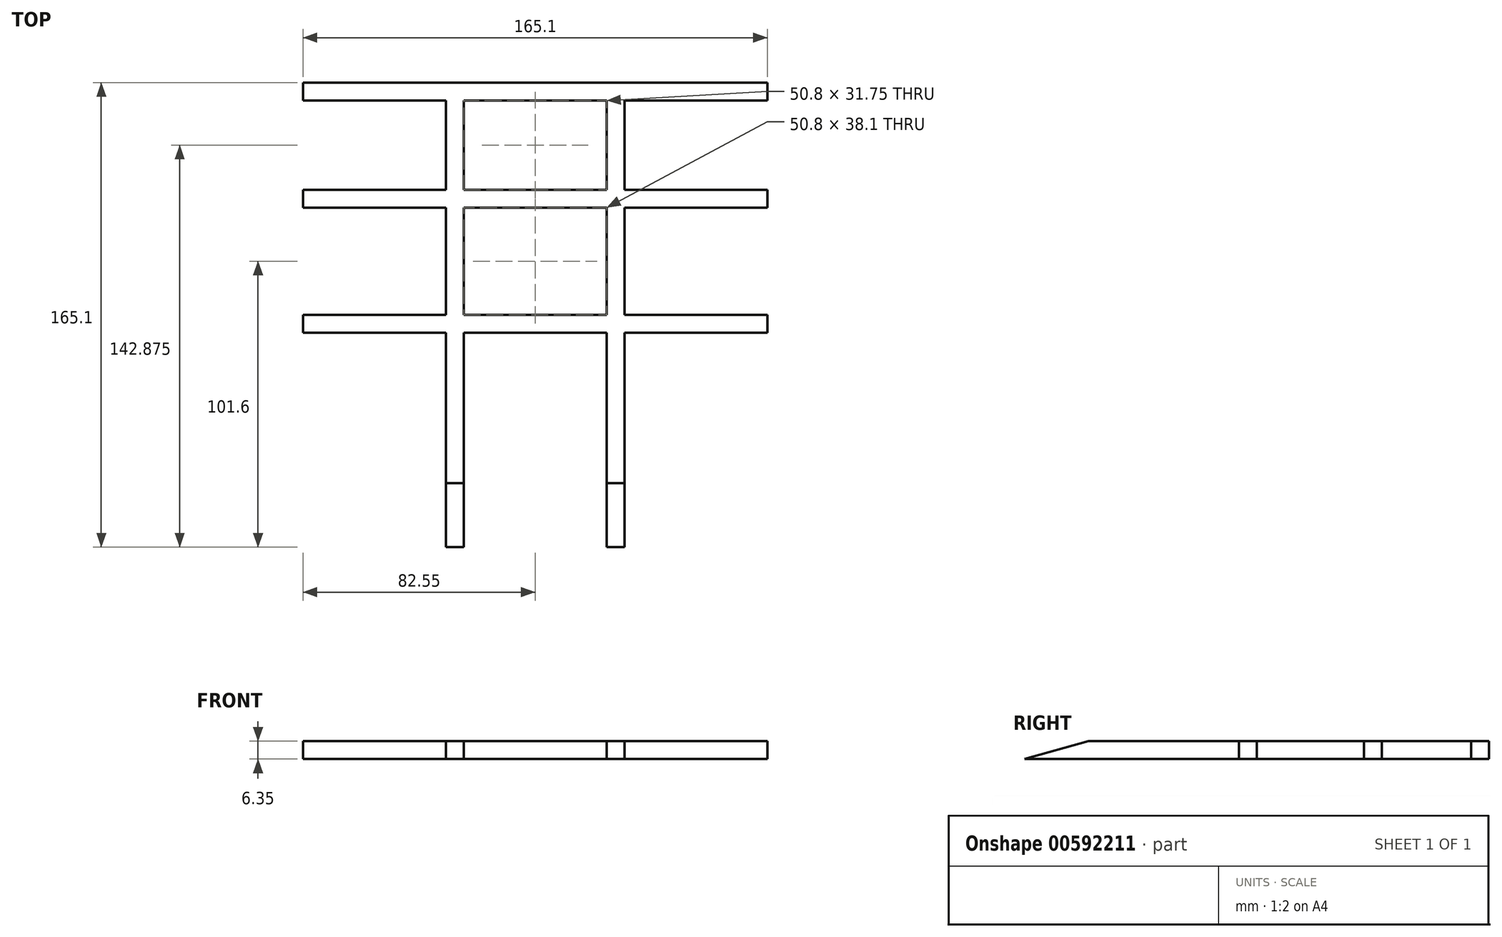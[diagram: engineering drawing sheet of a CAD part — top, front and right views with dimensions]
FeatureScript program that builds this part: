
annotation { "Feature Type Name" : "Feature", "Feature Type Description" : "" }
export const myFeature = defineFeature(function(context is Context, id is Id, definition is map)
    precondition{}
    {
        {
            var Q0;
            Q0=qCreatedBy(makeId("Top.planeOp"),FACE);
            var sketch = newSketch(context, id + "F0", { "sketchPlane" : qUnion([Q0])});
            skLineSegment(sketch, "E0.bottom", {"start": v(0, 0) * mm, "end": v(6.35, 0) * mm});
            skLineSegment(sketch, "E0.top", {"start": v(0, -76.2) * mm, "end": v(6.35, -76.2) * mm});
            skLineSegment(sketch, "E0.left", {"start": v(0, 0) * mm, "end": v(0, -76.2) * mm});
            skLineSegment(sketch, "E0.right", {"start": v(6.35, 0) * mm, "end": v(6.35, -76.2) * mm});
            skLineSegment(sketch, "E1.bottom", {"start": v(0, 0) * mm, "end": v(-50.8, 0) * mm});
            skLineSegment(sketch, "E1.top", {"start": v(0, 6.35) * mm, "end": v(-50.8, 6.35) * mm});
            skLineSegment(sketch, "E1.left", {"start": v(0, 0) * mm, "end": v(0, 6.35) * mm});
            skLineSegment(sketch, "E1.right", {"start": v(-50.8, 0) * mm, "end": v(-50.8, 6.35) * mm});
            skPoint(sketch, "E2.oppositeSnap0", {"position": v(3.18, -76.2) * mm});
            skLineSegment(sketch, "E2.bottom", {"start": v(-50.8, 0) * mm, "end": v(-57.15, 0) * mm});
            skLineSegment(sketch, "E2.top", {"start": v(-50.8, -76.2) * mm, "end": v(-57.15, -76.2) * mm});
            skLineSegment(sketch, "E2.left", {"start": v(-50.8, 0) * mm, "end": v(-50.8, -76.2) * mm});
            skLineSegment(sketch, "E2.right", {"start": v(-57.15, 0) * mm, "end": v(-57.15, -76.2) * mm});
            skLineSegment(sketch, "E3.bottom", {"start": v(-57.15, 0) * mm, "end": v(-107.95, 0) * mm});
            skLineSegment(sketch, "E3.top", {"start": v(-57.15, 6.35) * mm, "end": v(-107.95, 6.35) * mm});
            skLineSegment(sketch, "E3.left", {"start": v(-57.15, 0) * mm, "end": v(-57.15, 6.35) * mm});
            skLineSegment(sketch, "E3.right", {"start": v(-107.95, 0) * mm, "end": v(-107.95, 6.35) * mm});
            skLineSegment(sketch, "E4.bottom", {"start": v(6.35, 0) * mm, "end": v(57.15, 0) * mm});
            skLineSegment(sketch, "E4.top", {"start": v(6.35, 6.35) * mm, "end": v(57.15, 6.35) * mm});
            skLineSegment(sketch, "E4.left", {"start": v(6.35, 0) * mm, "end": v(6.35, 6.35) * mm});
            skLineSegment(sketch, "E4.right", {"start": v(57.15, 0) * mm, "end": v(57.15, 6.35) * mm});
            skLineSegment(sketch, "E5.bottom", {"start": v(-57.15, 6.35) * mm, "end": v(-50.8, 6.35) * mm});
            skLineSegment(sketch, "E5.top", {"start": v(-57.15, 44.45) * mm, "end": v(-50.8, 44.45) * mm});
            skLineSegment(sketch, "E5.left", {"start": v(-57.15, 6.35) * mm, "end": v(-57.15, 44.45) * mm});
            skLineSegment(sketch, "E5.right", {"start": v(-50.8, 6.35) * mm, "end": v(-50.8, 44.45) * mm});
            skLineSegment(sketch, "E6.bottom", {"start": v(0, 6.35) * mm, "end": v(6.35, 6.35) * mm});
            skLineSegment(sketch, "E6.top", {"start": v(0, 44.45) * mm, "end": v(6.35, 44.45) * mm});
            skLineSegment(sketch, "E6.left", {"start": v(0, 6.35) * mm, "end": v(0, 44.45) * mm});
            skLineSegment(sketch, "E6.right", {"start": v(6.35, 6.35) * mm, "end": v(6.35, 44.45) * mm});
            skLineSegment(sketch, "E7.bottom", {"start": v(-107.95, 44.45) * mm, "end": v(57.15, 44.45) * mm});
            skLineSegment(sketch, "E7.top", {"start": v(-107.95, 50.8) * mm, "end": v(57.15, 50.8) * mm});
            skLineSegment(sketch, "E7.left", {"start": v(-107.95, 44.45) * mm, "end": v(-107.95, 50.8) * mm});
            skLineSegment(sketch, "E7.right", {"start": v(57.15, 44.45) * mm, "end": v(57.15, 50.8) * mm});
            skLineSegment(sketch, "E8.MirrorCS", {"start": v(-57.15, 82.55) * mm, "end": v(-57.15, 44.45) * mm});
            skLineSegment(sketch, "E9.MirrorCS", {"start": v(-50.8, 82.55) * mm, "end": v(-50.8, 44.45) * mm});
            skLineSegment(sketch, "E10.MirrorCS", {"start": v(0, 82.55) * mm, "end": v(0, 44.45) * mm});
            skLineSegment(sketch, "E11.MirrorCS", {"start": v(6.35, 82.55) * mm, "end": v(6.35, 44.45) * mm});
            skLineSegment(sketch, "E12.MirrorCS", {"start": v(-57.15, 82.55) * mm, "end": v(-50.8, 82.55) * mm});
            skLineSegment(sketch, "E13.MirrorCS", {"start": v(0, 82.55) * mm, "end": v(6.35, 82.55) * mm});
            skLineSegment(sketch, "E14.bottom", {"start": v(-107.95, 82.55) * mm, "end": v(57.15, 82.55) * mm});
            skLineSegment(sketch, "E14.top", {"start": v(-107.95, 88.9) * mm, "end": v(57.15, 88.9) * mm});
            skLineSegment(sketch, "E14.left", {"start": v(-107.95, 82.55) * mm, "end": v(-107.95, 88.9) * mm});
            skLineSegment(sketch, "E14.right", {"start": v(57.15, 82.55) * mm, "end": v(57.15, 88.9) * mm});
            skSolve(sketch);
        }
        {
            var Q0;
            Q0=makeQuery(id+"F0.imprint","IMPRINT",FACE,{"disambiguationData":[TD([[makeQuery(id+"F0.imprint","IMPRINT",EDGE,{"derivedFrom":sQuery(id+"F0.wireOp",EDGE,"E14.top")}),-1.0]])]});
            var Q1;
            {var subQ0=sQuery(id+"F0.wireOp",EDGE,"E8.MirrorCS");var subQ1=sQuery(id+"F0.wireOp",EDGE,"E7.top");var subQ2=makeQuery(id+"F0.imprint","INTERSECT",VERTEX,{"derivedFrom":[subQ1,subQ0]});Q1=makeQuery(id+"F0.imprint","IMPRINT",FACE,{"disambiguationData":[TD([[makeQuery(id+"F0.imprint","IMPRINT",EDGE,{"disambiguationData":[TD([[subQ2,-1.0]])],"derivedFrom":subQ1}),1.0]])]});}
            var Q2;
            {var subQ0=sQuery(id+"F0.wireOp",EDGE,"E11.MirrorCS");var subQ1=sQuery(id+"F0.wireOp",EDGE,"E7.top");var subQ2=makeQuery(id+"F0.imprint","INTERSECT",VERTEX,{"derivedFrom":[subQ1,subQ0]});Q2=makeQuery(id+"F0.imprint","IMPRINT",FACE,{"disambiguationData":[TD([[makeQuery(id+"F0.imprint","IMPRINT",EDGE,{"disambiguationData":[TD([[subQ2,1.0]])],"derivedFrom":subQ1}),1.0]])]});}
            var Q3;
            {var subQ3=sQuery(id+"F0.wireOp",EDGE,"E7.right");Q3=makeQuery(id+"F0.imprint","IMPRINT",FACE,{"disambiguationData":[TD([[makeQuery(id+"F0.imprint","IMPRINT",EDGE,{"derivedFrom":subQ3}),1.0]])]});}
            var Q4;
            {var subQ3=sQuery(id+"F0.wireOp",EDGE,"E11.MirrorCS");var subQ5=sQuery(id+"F0.wireOp",EDGE,"E7.top");var subQ6=makeQuery(id+"F0.imprint","INTERSECT",VERTEX,{"derivedFrom":[subQ5,subQ3]});Q4=makeQuery(id+"F0.imprint","IMPRINT",FACE,{"disambiguationData":[TD([[makeQuery(id+"F0.imprint","IMPRINT",EDGE,{"disambiguationData":[TD([[subQ6,1.0]])],"derivedFrom":subQ5}),-1.0]])]});}
            var Q5;
            {var subQ0=sQuery(id+"F0.wireOp",EDGE,"E9.MirrorCS");var subQ5=sQuery(id+"F0.wireOp",EDGE,"E7.top");var subQ6=makeQuery(id+"F0.imprint","INTERSECT",VERTEX,{"derivedFrom":[subQ5,subQ0]});Q5=makeQuery(id+"F0.imprint","IMPRINT",FACE,{"disambiguationData":[TD([[makeQuery(id+"F0.imprint","IMPRINT",EDGE,{"disambiguationData":[TD([[subQ6,-1.0]])],"derivedFrom":subQ5}),-1.0]])]});}
            var Q6;
            {var subQ3=sQuery(id+"F0.wireOp",EDGE,"E7.left");Q6=makeQuery(id+"F0.imprint","IMPRINT",FACE,{"disambiguationData":[TD([[makeQuery(id+"F0.imprint","IMPRINT",EDGE,{"derivedFrom":subQ3}),-1.0]])]});}
            var Q7;
            {var subQ0=sQuery(id+"F0.wireOp",EDGE,"E8.MirrorCS");var subQ5=sQuery(id+"F0.wireOp",EDGE,"E7.top");var subQ6=makeQuery(id+"F0.imprint","INTERSECT",VERTEX,{"derivedFrom":[subQ5,subQ0]});Q7=makeQuery(id+"F0.imprint","IMPRINT",FACE,{"disambiguationData":[TD([[makeQuery(id+"F0.imprint","IMPRINT",EDGE,{"disambiguationData":[TD([[subQ6,-1.0]])],"derivedFrom":subQ5}),-1.0]])]});}
            var Q8;
            Q8=makeQuery(id+"F0.imprint","IMPRINT",FACE,{"disambiguationData":[TD([[makeQuery(id+"F0.imprint","IMPRINT",EDGE,{"derivedFrom":sQuery(id+"F0.wireOp",EDGE,"E5.bottom")}),1.0]])]});
            var Q9;
            Q9=makeQuery(id+"F0.imprint","IMPRINT",FACE,{"disambiguationData":[TD([[makeQuery(id+"F0.imprint","IMPRINT",EDGE,{"derivedFrom":sQuery(id+"F0.wireOp",EDGE,"E6.bottom")}),1.0]])]});
            var Q10;
            Q10=makeQuery(id+"F0.imprint","IMPRINT",FACE,{"disambiguationData":[TD([[makeQuery(id+"F0.imprint","IMPRINT",EDGE,{"derivedFrom":sQuery(id+"F0.wireOp",EDGE,"E0.bottom")}),-1.0]])]});
            var Q11;
            Q11=makeQuery(id+"F0.imprint","IMPRINT",FACE,{"disambiguationData":[TD([[makeQuery(id+"F0.imprint","IMPRINT",EDGE,{"derivedFrom":sQuery(id+"F0.wireOp",EDGE,"E0.bottom")}),1.0]])]});
            var Q12;
            Q12=makeQuery(id+"F0.imprint","IMPRINT",FACE,{"disambiguationData":[TD([[makeQuery(id+"F0.imprint","IMPRINT",EDGE,{"derivedFrom":sQuery(id+"F0.wireOp",EDGE,"E4.bottom")}),1.0]])]});
            var Q13;
            Q13=makeQuery(id+"F0.imprint","IMPRINT",FACE,{"disambiguationData":[TD([[makeQuery(id+"F0.imprint","IMPRINT",EDGE,{"derivedFrom":sQuery(id+"F0.wireOp",EDGE,"E1.bottom")}),-1.0]])]});
            var Q14;
            Q14=makeQuery(id+"F0.imprint","IMPRINT",FACE,{"disambiguationData":[TD([[makeQuery(id+"F0.imprint","IMPRINT",EDGE,{"derivedFrom":sQuery(id+"F0.wireOp",EDGE,"E1.right")}),1.0]])]});
            var Q15;
            Q15=makeQuery(id+"F0.imprint","IMPRINT",FACE,{"disambiguationData":[TD([[makeQuery(id+"F0.imprint","IMPRINT",EDGE,{"derivedFrom":sQuery(id+"F0.wireOp",EDGE,"E2.bottom")}),1.0]])]});
            var Q16;
            Q16=makeQuery(id+"F0.imprint","IMPRINT",FACE,{"disambiguationData":[TD([[makeQuery(id+"F0.imprint","IMPRINT",EDGE,{"derivedFrom":sQuery(id+"F0.wireOp",EDGE,"E3.bottom")}),-1.0]])]});
            extrude(context, id + "F1", {"entities" : qUnion([Q0, Q1, Q2, Q3, Q4, Q5, Q6, Q7, Q8, Q9, Q10, Q11, Q12, Q13, Q14, Q15, Q16]), "depth" : 6.35 * mm, "offsetDistance" : 25.4 * mm});
        }
        {
            var Q0;
            Q0=makeQuery(id+"F1.opExtrude","SWEPT_FACE",FACE,{"disambiguationData":[OSD([sQuery(id+"F0.wireOp",EDGE,"E2.right")])]});
            var sketch = newSketch(context, id + "F2", { "sketchPlane" : qUnion([Q0])});
            skLineSegment(sketch, "E15", {"start": v(76.2, 0) * mm, "end": v(53.46, 6.35) * mm});
            skLineSegment(sketch, "E16", {"start": v(53.46, 6.35) * mm, "end": v(76.2, 6.35) * mm});
            skLineSegment(sketch, "E17", {"start": v(76.2, 6.35) * mm, "end": v(76.2, 0) * mm});
            skSolve(sketch);
        }
        {
            var Q0;
            Q0=makeQuery(id+"F2.imprint","IMPRINT",FACE,{"disambiguationData":[TD([[makeQuery(id+"F2.imprint","IMPRINT",EDGE,{"derivedFrom":sQuery(id+"F2.wireOp",EDGE,"E15")}),-1.0]])]});
            var Q1;
            Q1=makeQuery(id+"F1.opExtrude","SWEPT_FACE",FACE,{"disambiguationData":[OSD([sQuery(id+"F0.wireOp",EDGE,"E0.right")])]});
            extrude(context, id + "F3", {"entities" : qUnion([Q0]), "operationType" : NewBodyOperationType.REMOVE, "endBound" : BoundingType.UP_TO_SURFACE, "oppositeDirection" : true, "depth" : 25.4 * mm, "endBoundEntityFace" : qUnion([Q1]), "offsetDistance" : 25.4 * mm});
        }
    });
